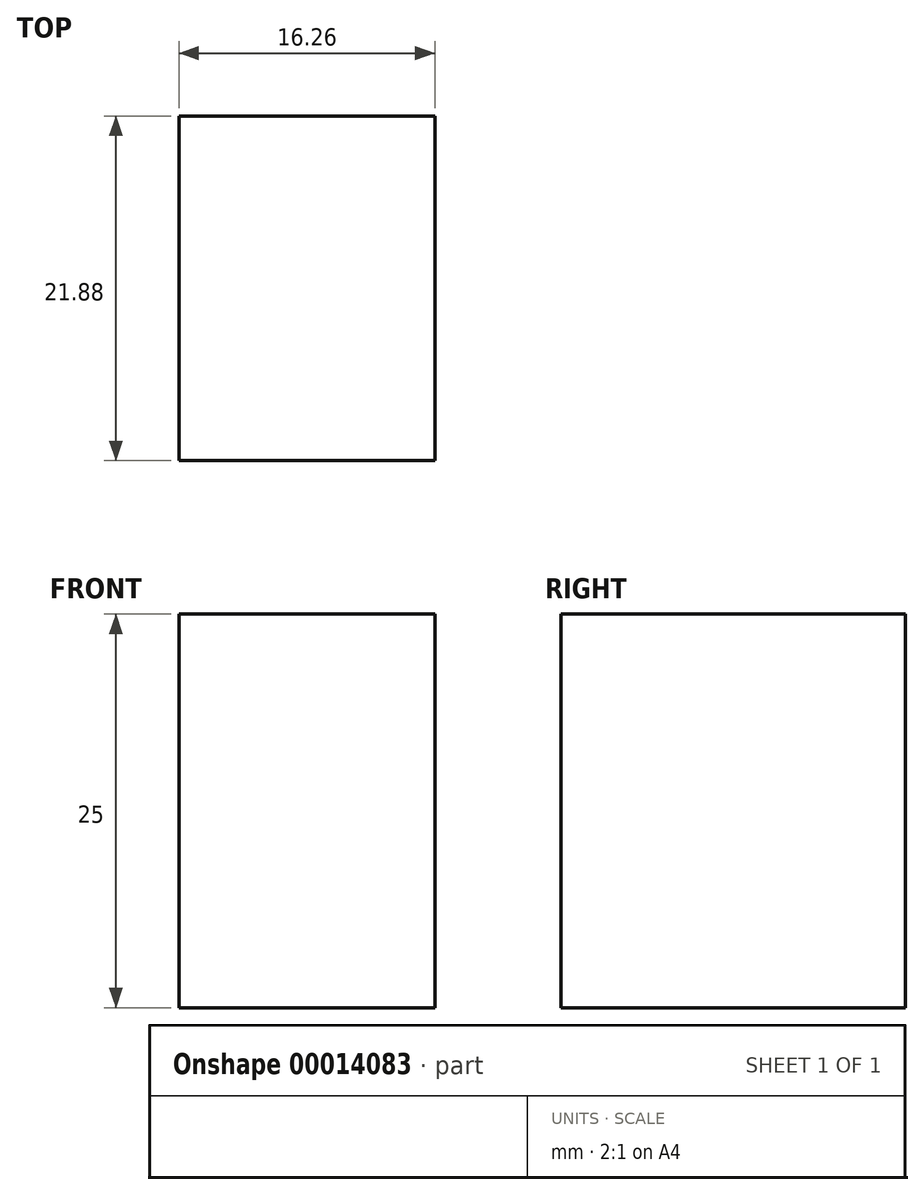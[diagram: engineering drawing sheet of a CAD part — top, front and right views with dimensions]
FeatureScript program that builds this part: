
annotation { "Feature Type Name" : "Feature", "Feature Type Description" : "" }
export const myFeature = defineFeature(function(context is Context, id is Id, definition is map)
    precondition{}
    {
        {
            var Q0;
            Q0=qCreatedBy(makeId("Front.planeOp"),FACE);
            var sketch = newSketch(context, id + "F0", { "sketchPlane" : qUnion([Q0])});
            skLineSegment(sketch, "E0", {"start": v(0, 0) * mm, "end": v(0, 450) * mm});
            skLineSegment(sketch, "E1", {"start": v(0, 0) * mm, "end": v(450, 0) * mm});
            skSolve(sketch);
        }
        {
            var Q0;
            Q0=qCreatedBy(makeId("Top.planeOp"),FACE);
            var sketch = newSketch(context, id + "F1", { "sketchPlane" : qUnion([Q0])});
            skLineSegment(sketch, "E2.rect.bottom", {"start": v(8.13, 10.94) * mm, "end": v(-8.13, 10.94) * mm});
            skLineSegment(sketch, "E2.rect.top", {"start": v(8.13, -10.94) * mm, "end": v(-8.13, -10.94) * mm});
            skLineSegment(sketch, "E2.rect.left", {"start": v(8.13, 10.94) * mm, "end": v(8.13, -10.94) * mm});
            skLineSegment(sketch, "E2.rect.right", {"start": v(-8.13, 10.94) * mm, "end": v(-8.13, -10.94) * mm});
            skPoint(sketch, "E2.rect.middle", {"position": v(0, 0) * mm});
            skSolve(sketch);
        }
        {
            var Q0;
            Q0 = qSketchRegion(id + "F1", true);
            extrude(context, id + "F2", {"entities" : qUnion([Q0]), "depth" : 25 * mm, "symmetric" : true});
        }
    });
